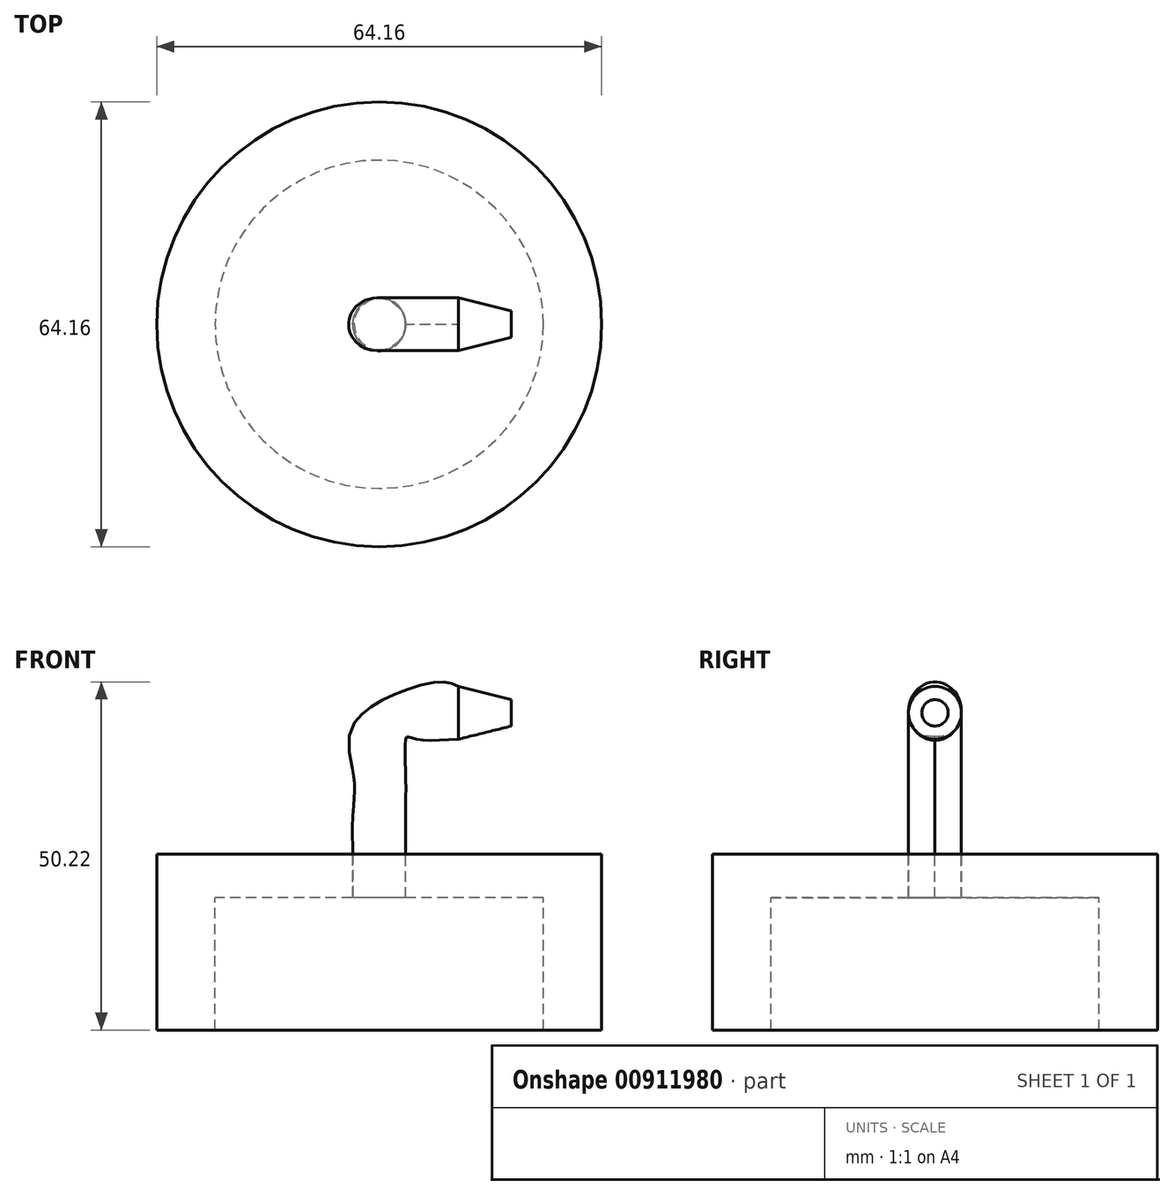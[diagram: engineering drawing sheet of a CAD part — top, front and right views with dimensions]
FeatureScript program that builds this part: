
annotation { "Feature Type Name" : "Feature", "Feature Type Description" : "" }
export const myFeature = defineFeature(function(context is Context, id is Id, definition is map)
    precondition{}
    {
        {
            var Q0;
            Q0=qCreatedBy(makeId("Front.planeOp"),FACE);
            var sketch = newSketch(context, id + "F0", { "sketchPlane" : qUnion([Q0])});
            skLineSegment(sketch, "E0.bottom", {"start": v(-32.08, 6.3) * mm, "end": v(-23.68, 6.3) * mm});
            skLineSegment(sketch, "E0.top", {"start": v(-32.08, -19.1) * mm, "end": v(-23.68, -19.1) * mm});
            skLineSegment(sketch, "E0.left", {"start": v(-32.08, 6.3) * mm, "end": v(-32.08, -19.1) * mm});
            skLineSegment(sketch, "E0.right", {"start": v(-23.68, 6.3) * mm, "end": v(-23.68, -19.1) * mm});
            skLineSegment(sketch, "E1.bottom", {"start": v(-23.68, 6.3) * mm, "end": v(-3.82, 6.3) * mm});
            skLineSegment(sketch, "E1.top", {"start": v(-23.68, 0) * mm, "end": v(-3.82, 0) * mm});
            skLineSegment(sketch, "E1.left", {"start": v(-23.68, 6.3) * mm, "end": v(-23.68, 0) * mm});
            skLineSegment(sketch, "E1.right", {"start": v(-3.82, 6.3) * mm, "end": v(-3.82, 0) * mm});
            skLineSegment(sketch, "E2", {"start": v(0, 12.89) * mm, "end": v(0, -13.08) * mm, "construction": true});
            skLineSegment(sketch, "E3", {"start": v(0, 3.56) * mm, "end": v(-3.81, 3.56) * mm, "construction": true});
            skSolve(sketch);
        }
        {
            var Q0;
            {var subQ0=sQuery(id+"F0.wireOp",EDGE,"E1.bottom");var subQ2=sQuery(id+"F0.wireOp",EDGE,"E0.bottom");Q0=qUnion([makeQuery(id+"F0.imprint","IMPRINT",FACE,{"disambiguationData":[TD([[makeQuery(id+"F0.imprint","IMPRINT",EDGE,{"derivedFrom":subQ2}),-1.0]])]}),makeQuery(id+"F0.imprint","IMPRINT",FACE,{"disambiguationData":[TD([[makeQuery(id+"F0.imprint","IMPRINT",EDGE,{"derivedFrom":subQ0}),-1.0]])]})]);}
            var Q1;
            Q1=sQuery(id+"F0.wireOp",EDGE,"E2");
            revolve(context, id + "F1", {"surfaceOperationType" : NewSurfaceOperationType.NEW, "entities" : qUnion([Q0]), "axis" : qUnion([Q1]), "revolveType" : RevolveType.FULL});
        }
        {
            var Q0;
            Q0=qCreatedBy(makeId("Top.planeOp"),FACE);
            var sketch = newSketch(context, id + "F2", { "sketchPlane" : qUnion([Q0])});
            skCircle(sketch, "E4", {"center": v(0, 0) * mm, "radius": 3.81 * mm});
            skSolve(sketch);
        }
        {
            var Q0;
            Q0=qCreatedBy(makeId("Front.planeOp"),FACE);
            var sketch = newSketch(context, id + "F3", { "sketchPlane" : qUnion([Q0])});
            skLineSegment(sketch, "E5", {"start": v(0, 0) * mm, "end": v(0, 22.86) * mm});
            skLineSegment(sketch, "E6", {"start": v(0, 22.86) * mm, "end": v(3.81, 22.86) * mm, "construction": true});
            skArc(sketch, "E7", {"start": v(0, 22.86) * mm, "mid": v(1.12, 25.55) * mm, "end": v(3.81, 26.67) * mm});
            skLineSegment(sketch, "E8", {"start": v(3.81, 26.67) * mm, "end": v(11.43, 26.67) * mm});
            skSolve(sketch);
        }
        {
            var Q0;
            Q0=sQuery(id+"F3.wireOp",VERTEX,"E8.end");
            var Q1;
            Q1=sQuery(id+"F3.wireOp",EDGE,"E8");
            cPlane(context, id + "F4", {"entities" : qUnion([Q0, Q1]), "cplaneType" : CPlaneType.CURVE_POINT, "offset" : 25.4 * mm, "width" : 152.4 * mm, "height" : 152.4 * mm});
        }
        {
            var Q0;
            Q0=qCreatedBy(id+"F4.planeOp",FACE);
            var sketch = newSketch(context, id + "F5", { "sketchPlane" : qUnion([Q0])});
            skCircle(sketch, "E9", {"center": v(0, 26.67) * mm, "radius": 3.81 * mm});
            skSolve(sketch);
        }
        {
            var Q0;
            Q0=sQuery(id+"F3.wireOp",EDGE,"E8");
            var Q1;
            Q1=sQuery(id+"F3.wireOp",EDGE,"E7");
            var Q2;
            Q2=sQuery(id+"F3.wireOp",EDGE,"E5");
            var Q3;
            Q3=makeQuery(id+"F2.imprint","IMPRINT",FACE,{"disambiguationData":[TD([[makeQuery(id+"F2.imprint","IMPRINT",EDGE,{"derivedFrom":sQuery(id+"F2.wireOp",EDGE,"E4")}),1.0]])]});
            var Q4;
            Q4=makeQuery(id+"F5.imprint","IMPRINT",FACE,{"disambiguationData":[TD([[makeQuery(id+"F5.imprint","IMPRINT",EDGE,{"derivedFrom":sQuery(id+"F5.wireOp",EDGE,"E9")}),1.0]])]});
            var Q5;
            Q5=sQuery(id+"F5.wireOp",EDGE,"E9");
            var Q6;
            Q6=sQuery(id+"F2.wireOp",EDGE,"E4");
            loft(context, id + "F6", {"addSections" : true, "spine" : qUnion([Q0, Q1, Q2]), "sectionCount" : 5, "sheetProfilesArray" : [{ "sheetProfileEntities" : qUnion([Q3]) }, { "sheetProfileEntities" : qUnion([Q4]) }], "wireProfilesArray" : [{ "wireProfileEntities" : qUnion([Q5]) }, { "wireProfileEntities" : qUnion([Q6]) }]});
        }
        {
            var Q0;
            Q0=qCreatedBy(id+"F4.planeOp",FACE);
            cPlane(context, id + "F7", {"entities" : qUnion([Q0]), "cplaneType" : CPlaneType.OFFSET, "offset" : 7.62 * mm, "width" : 152.4 * mm, "height" : 152.4 * mm});
        }
        {
            var Q0;
            Q0=qCreatedBy(id+"F7.planeOp",FACE);
            var sketch = newSketch(context, id + "F8", { "sketchPlane" : qUnion([Q0])});
            skCircle(sketch, "E10", {"center": v(0, 26.67) * mm, "radius": 1.9 * mm});
            skSolve(sketch);
        }
        {
            var Q0;
            Q0=makeQuery(id+"F5.imprint","IMPRINT",FACE,{"disambiguationData":[TD([[makeQuery(id+"F5.imprint","IMPRINT",EDGE,{"derivedFrom":sQuery(id+"F5.wireOp",EDGE,"E9")}),1.0]])]});
            var Q1;
            Q1=makeQuery(id+"F8.imprint","IMPRINT",FACE,{"disambiguationData":[TD([[makeQuery(id+"F8.imprint","IMPRINT",EDGE,{"derivedFrom":sQuery(id+"F8.wireOp",EDGE,"E10")}),1.0]])]});
            loft(context, id + "F9", {"operationType" : NewBodyOperationType.ADD, "sheetProfilesArray" : [{ "sheetProfileEntities" : qUnion([Q0]) }, { "sheetProfileEntities" : qUnion([Q1]) }]});
        }
    });
